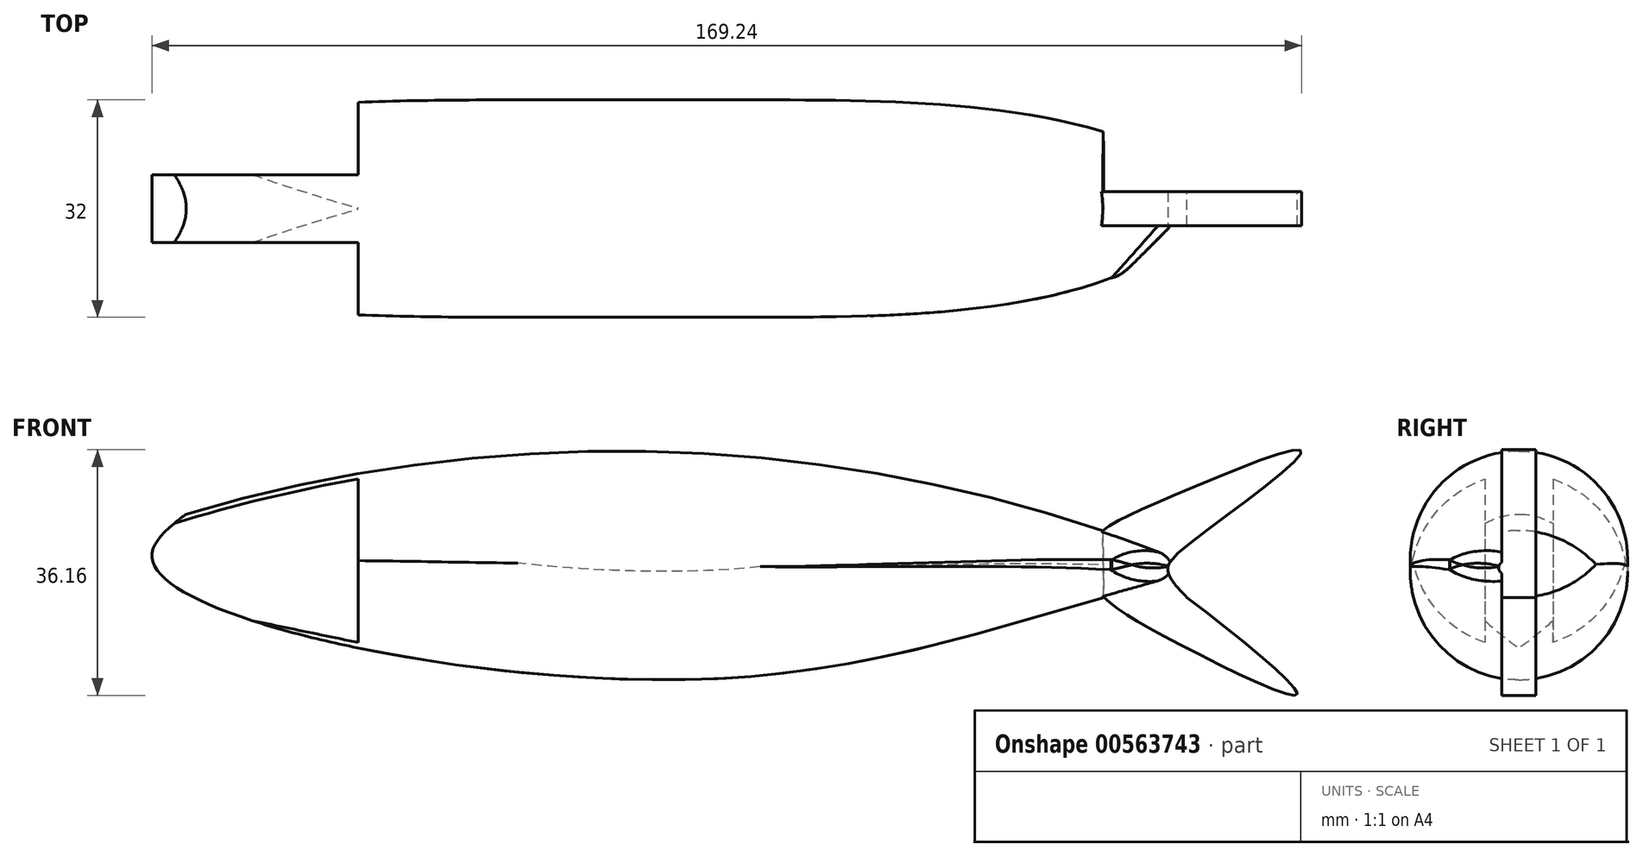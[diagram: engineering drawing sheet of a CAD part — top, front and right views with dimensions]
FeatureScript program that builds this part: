
annotation { "Feature Type Name" : "Feature", "Feature Type Description" : "" }
export const myFeature = defineFeature(function(context is Context, id is Id, definition is map)
    precondition{}
    {
        {
            var Q0;
            Q0=qCreatedBy(makeId("Front.planeOp"),FACE);
            var sketch = newSketch(context, id + "F0", { "sketchPlane" : qUnion([Q0])});
            skArc(sketch, "E0", {"start": v(111.88, 17) * mm, "mid": v(44.62, 28.67) * mm, "end": v(-23.02, 19.44) * mm});
            skLineSegment(sketch, "E1", {"start": v(111.88, 17) * mm, "end": v(112.06, 7.19) * mm});
            skFitSpline(sketch, "E2", {"points": [v(-23.02, 19.44) * mm, v(-28.07, 13.13) * mm, v(-16.09, 4.72) * mm, v(55.6, -4.74) * mm, v(112.06, 7.19) * mm], "startDerivative": vector(-71.7, -52.58) * mm, "endDerivative": vector(154.39, 43.5) * mm});
            skFitSpline(sketch, "E3", {"points": [v(112.06, 7.19) * mm, v(121.35, 1.25) * mm, v(140.45, -7.16) * mm, v(124.3, 7.19) * mm], "startDerivative": vector(24.22, -21.87) * mm, "endDerivative": vector(-61.4, 47.24) * mm});
            skFitSpline(sketch, "E4", {"points": [v(124.3, 7.19) * mm, v(123.75, 14.34) * mm, v(141.15, 28.67) * mm, v(122.45, 22.24) * mm, v(111.88, 17) * mm], "startDerivative": vector(-67.34, 66.85) * mm, "endDerivative": vector(-29.29, -22.17) * mm});
            skLineSegment(sketch, "E5", {"start": v(2.3, 25.4) * mm, "end": v(2.3, -0.26) * mm});
            skSolve(sketch);
        }
        {
            var Q0;
            Q0=makeQuery(id+"F0.imprint","IMPRINT",FACE,{"disambiguationData":[TD([[makeQuery(id+"F0.imprint","IMPRINT",EDGE,{"derivedFrom":sQuery(id+"F0.wireOp",EDGE,"E0")}),1.0]])]});
            extrude(context, id + "F1", {"entities" : qUnion([Q0]), "depth" : 5 * mm, "offsetDistance" : 25 * mm, "hasSecondDirection" : true, "secondDirectionOppositeDirection" : true, "secondDirectionDepth" : 5 * mm});
        }
        {
            var Q0;
            Q0=makeQuery(id+"F0.imprint","IMPRINT",FACE,{"disambiguationData":[TD([[makeQuery(id+"F0.imprint","IMPRINT",EDGE,{"derivedFrom":sQuery(id+"F0.wireOp",EDGE,"E1")}),1.0]])]});
            extrude(context, id + "F2", {"entities" : qUnion([Q0]), "operationType" : NewBodyOperationType.ADD, "depth" : 2.5 * mm, "offsetDistance" : 25 * mm, "hasSecondDirection" : true, "secondDirectionOppositeDirection" : true, "secondDirectionDepth" : 2.5 * mm});
        }
        {
            var Q0;
            {var subQ0=sQuery(id+"F0.wireOp",EDGE,"E1");Q0=makeQuery(id+"F0.imprint","IMPRINT",FACE,{"disambiguationData":[TD([[makeQuery(id+"F0.imprint","IMPRINT",EDGE,{"derivedFrom":subQ0}),-1.0]])]});}
            extrude(context, id + "F3", {"entities" : qUnion([Q0]), "operationType" : NewBodyOperationType.ADD, "depth" : 16 * mm, "offsetDistance" : 25 * mm, "hasSecondDirection" : true, "secondDirectionOppositeDirection" : true, "secondDirectionDepth" : 16 * mm});
        }
        {
            var Q0;
            Q0=makeQuery(id+"F3.opExtrude","CAP_FACE",FACE,{"disambiguationData":[OSD([sQuery(id+"F0.wireOp",EDGE,"E0"),sQuery(id+"F0.wireOp",EDGE,"E1"),sQuery(id+"F0.wireOp",EDGE,"E2"),sQuery(id+"F0.wireOp",EDGE,"E5")])],"isStart":false});
            var Q1;
            Q1=makeQuery(id+"F3.opExtrude","CAP_FACE",FACE,{"disambiguationData":[OSD([sQuery(id+"F0.wireOp",EDGE,"E0"),sQuery(id+"F0.wireOp",EDGE,"E1"),sQuery(id+"F0.wireOp",EDGE,"E2"),sQuery(id+"F0.wireOp",EDGE,"E5")])],"isStart":true});
            fillet(context, id + "F4", {"entities" : qUnion([Q0, Q1]), "radius" : 15.95 * mm, "tangentPropagation" : true, "allowEdgeOverflow" : false});
        }
        {
            var Q0;
            Q0=makeQuery(id+"F2.opExtrude","CAP_EDGE",EDGE,{"disambiguationData":[OSD([sQuery(id+"F0.wireOp",EDGE,"E1")])],"isStart":false});
            var Q1;
            Q1=makeQuery(id+"F2.opExtrude","CAP_EDGE",EDGE,{"disambiguationData":[OSD([sQuery(id+"F0.wireOp",EDGE,"E1")])],"isStart":true});
            chamfer(context, id + "F5", {"entities" : qUnion([Q0, Q1]), "width" : 10 * mm, "tangentPropagation" : true});
        }
        {
            var Q0;
            {var subQ0=sQuery(id+"F0.wireOp",EDGE,"E0");Q0=makeQuery(id+"F5.opChamfer","BLEND_EDGE",EDGE,{"blendedFrom":[makeQuery(id+"F2.opExtrude","CAP_EDGE",EDGE,{"disambiguationData":[OSD([sQuery(id+"F0.wireOp",EDGE,"E1")])],"isStart":false}),makeQuery(id+"F4.opFillet","BLEND_FACE",FACE,{"disambiguationData":[OSD([subQ0]),TDD([makeQuery(id+"F3.opExtrude","CAP_EDGE",EDGE,{"disambiguationData":[OSD([subQ0])],"isStart":false})])]})],"blendedInto":[makeQuery(id+"F4.opFillet","BLEND_FACE",FACE,{"disambiguationData":[OSD([subQ0]),TDD([makeQuery(id+"F3.opExtrude","CAP_EDGE",EDGE,{"disambiguationData":[OSD([subQ0])],"isStart":false})])]})]});}
            var Q1;
            {var subQ0=sQuery(id+"F0.wireOp",EDGE,"E2");Q1=makeQuery(id+"F5.opChamfer","BLEND_EDGE",EDGE,{"blendedFrom":[makeQuery(id+"F2.opExtrude","CAP_EDGE",EDGE,{"disambiguationData":[OSD([sQuery(id+"F0.wireOp",EDGE,"E1")])],"isStart":false}),makeQuery(id+"F4.opFillet","BLEND_FACE",FACE,{"disambiguationData":[OSD([subQ0]),TDD([makeQuery(id+"F3.opExtrude","CAP_EDGE",EDGE,{"disambiguationData":[OSD([subQ0])],"isStart":false})])]})],"blendedInto":[makeQuery(id+"F4.opFillet","BLEND_FACE",FACE,{"disambiguationData":[OSD([subQ0]),TDD([makeQuery(id+"F3.opExtrude","CAP_EDGE",EDGE,{"disambiguationData":[OSD([subQ0])],"isStart":false})])]})]});}
            var Q2;
            {var subQ0=sQuery(id+"F0.wireOp",EDGE,"E0");Q2=makeQuery(id+"F5.opChamfer","BLEND_EDGE",EDGE,{"blendedFrom":[makeQuery(id+"F2.opExtrude","CAP_EDGE",EDGE,{"disambiguationData":[OSD([sQuery(id+"F0.wireOp",EDGE,"E1")])],"isStart":true}),makeQuery(id+"F4.opFillet","BLEND_FACE",FACE,{"disambiguationData":[OSD([subQ0]),TDD([makeQuery(id+"F3.opExtrude","CAP_EDGE",EDGE,{"disambiguationData":[OSD([subQ0])],"isStart":true})])]})],"blendedInto":[makeQuery(id+"F4.opFillet","BLEND_FACE",FACE,{"disambiguationData":[OSD([subQ0]),TDD([makeQuery(id+"F3.opExtrude","CAP_EDGE",EDGE,{"disambiguationData":[OSD([subQ0])],"isStart":true})])]})]});}
            var Q3;
            {var subQ0=sQuery(id+"F0.wireOp",EDGE,"E2");Q3=makeQuery(id+"F5.opChamfer","BLEND_EDGE",EDGE,{"blendedFrom":[makeQuery(id+"F2.opExtrude","CAP_EDGE",EDGE,{"disambiguationData":[OSD([sQuery(id+"F0.wireOp",EDGE,"E1")])],"isStart":true}),makeQuery(id+"F4.opFillet","BLEND_FACE",FACE,{"disambiguationData":[OSD([subQ0]),TDD([makeQuery(id+"F3.opExtrude","CAP_EDGE",EDGE,{"disambiguationData":[OSD([subQ0])],"isStart":true})])]})],"blendedInto":[makeQuery(id+"F4.opFillet","BLEND_FACE",FACE,{"disambiguationData":[OSD([subQ0]),TDD([makeQuery(id+"F3.opExtrude","CAP_EDGE",EDGE,{"disambiguationData":[OSD([subQ0])],"isStart":true})])]})]});}
            fillet(context, id + "F6", {"entities" : qUnion([Q0, Q1, Q2, Q3]), "radius" : 2.1 * mm, "tangentPropagation" : true, "allowEdgeOverflow" : false});
        }
        {
            var Q0;
            {var subQ0=sQuery(id+"F0.wireOp",EDGE,"E2");var subQ1=makeQuery(id+"F2.opExtrude","CAP_EDGE",EDGE,{"disambiguationData":[OSD([sQuery(id+"F0.wireOp",EDGE,"E1")])],"isStart":false});var subQ2=sQuery(id+"F0.wireOp",EDGE,"E0");Q0=makeQuery(id+"F6.opFillet","BLEND_EDGE",EDGE,{"blendedFrom":[makeQuery(id+"F5.opChamfer","BLEND_EDGE",EDGE,{"blendedFrom":[subQ1,makeQuery(id+"F4.opFillet","BLEND_FACE",FACE,{"disambiguationData":[OSD([subQ2]),TDD([makeQuery(id+"F3.opExtrude","CAP_EDGE",EDGE,{"disambiguationData":[OSD([subQ2])],"isStart":false})])]})],"blendedInto":[makeQuery(id+"F4.opFillet","BLEND_FACE",FACE,{"disambiguationData":[OSD([subQ2]),TDD([makeQuery(id+"F3.opExtrude","CAP_EDGE",EDGE,{"disambiguationData":[OSD([subQ2])],"isStart":false})])]})]}),makeQuery(id+"F5.opChamfer","BLEND_EDGE",EDGE,{"blendedFrom":[subQ1,makeQuery(id+"F4.opFillet","BLEND_FACE",FACE,{"disambiguationData":[OSD([subQ0]),TDD([makeQuery(id+"F3.opExtrude","CAP_EDGE",EDGE,{"disambiguationData":[OSD([subQ0])],"isStart":false})])]})],"blendedInto":[makeQuery(id+"F4.opFillet","BLEND_FACE",FACE,{"disambiguationData":[OSD([subQ0]),TDD([makeQuery(id+"F3.opExtrude","CAP_EDGE",EDGE,{"disambiguationData":[OSD([subQ0])],"isStart":false})])]})]})],"blendedInto":[]});}
            var Q1;
            {var subQ0=sQuery(id+"F0.wireOp",EDGE,"E2");var subQ1=makeQuery(id+"F2.opExtrude","CAP_EDGE",EDGE,{"disambiguationData":[OSD([sQuery(id+"F0.wireOp",EDGE,"E1")])],"isStart":true});var subQ2=sQuery(id+"F0.wireOp",EDGE,"E0");Q1=makeQuery(id+"F6.opFillet","BLEND_EDGE",EDGE,{"blendedFrom":[makeQuery(id+"F5.opChamfer","BLEND_EDGE",EDGE,{"blendedFrom":[subQ1,makeQuery(id+"F4.opFillet","BLEND_FACE",FACE,{"disambiguationData":[OSD([subQ2]),TDD([makeQuery(id+"F3.opExtrude","CAP_EDGE",EDGE,{"disambiguationData":[OSD([subQ2])],"isStart":true})])]})],"blendedInto":[makeQuery(id+"F4.opFillet","BLEND_FACE",FACE,{"disambiguationData":[OSD([subQ2]),TDD([makeQuery(id+"F3.opExtrude","CAP_EDGE",EDGE,{"disambiguationData":[OSD([subQ2])],"isStart":true})])]})]}),makeQuery(id+"F5.opChamfer","BLEND_EDGE",EDGE,{"blendedFrom":[subQ1,makeQuery(id+"F4.opFillet","BLEND_FACE",FACE,{"disambiguationData":[OSD([subQ0]),TDD([makeQuery(id+"F3.opExtrude","CAP_EDGE",EDGE,{"disambiguationData":[OSD([subQ0])],"isStart":true})])]})],"blendedInto":[makeQuery(id+"F4.opFillet","BLEND_FACE",FACE,{"disambiguationData":[OSD([subQ0]),TDD([makeQuery(id+"F3.opExtrude","CAP_EDGE",EDGE,{"disambiguationData":[OSD([subQ0])],"isStart":true})])]})]})],"blendedInto":[]});}
            chamfer(context, id + "F7", {"entities" : qUnion([Q0, Q1]), "width" : 1 * mm, "tangentPropagation" : true});
        }
    });
